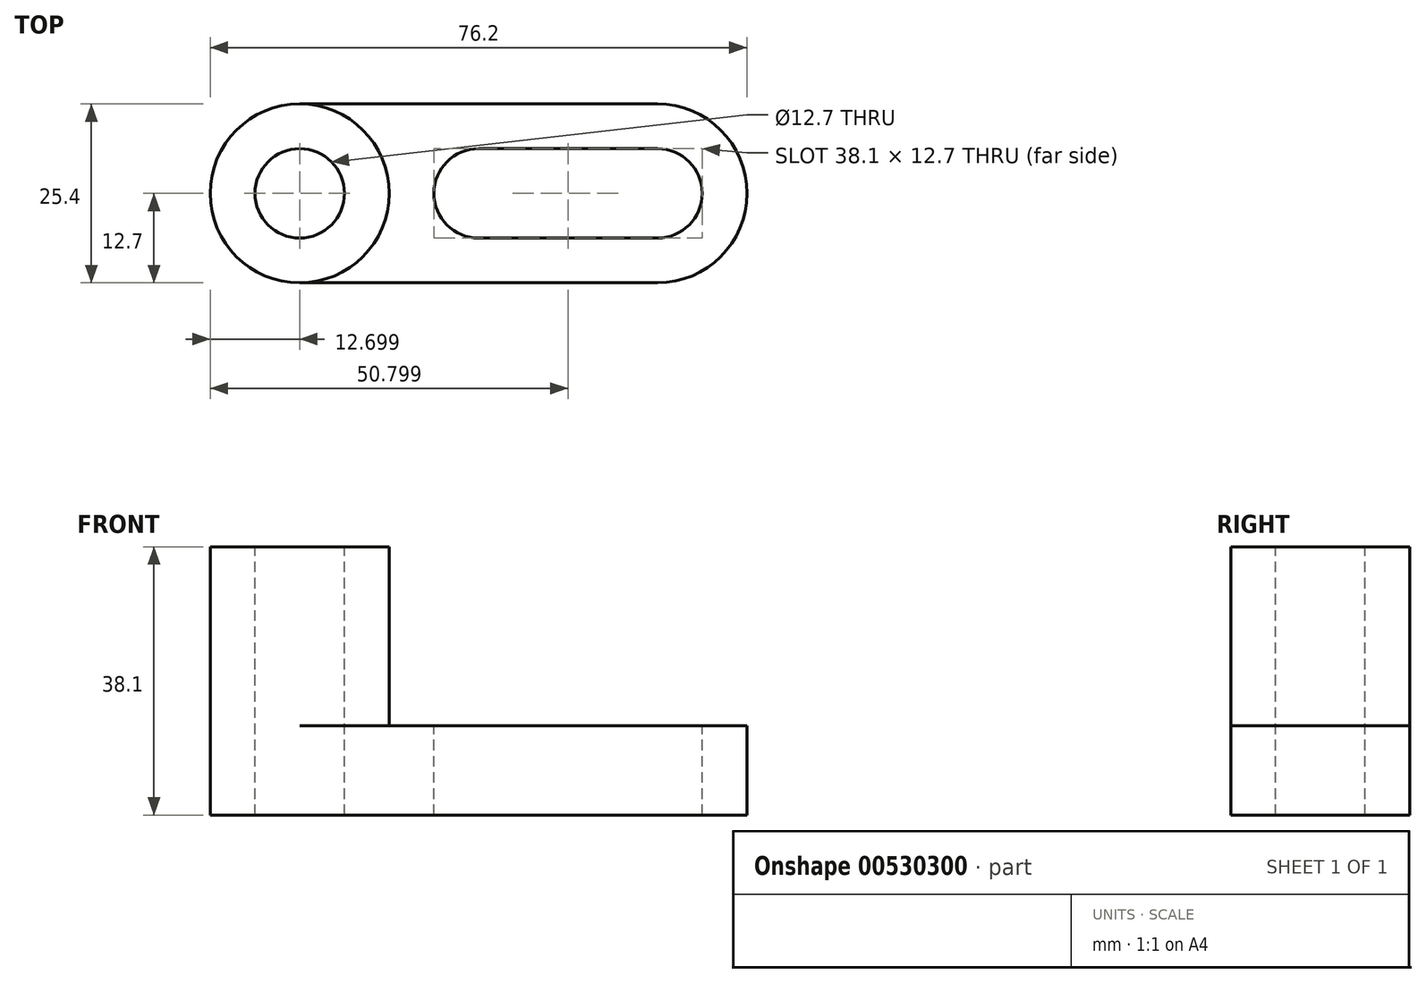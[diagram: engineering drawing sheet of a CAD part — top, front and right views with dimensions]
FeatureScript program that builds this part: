
annotation { "Feature Type Name" : "Feature", "Feature Type Description" : "" }
export const myFeature = defineFeature(function(context is Context, id is Id, definition is map)
    precondition{}
    {
        {
            var Q0;
            Q0=qCreatedBy(makeId("Front.planeOp"),FACE);
            var sketch = newSketch(context, id + "F0", { "sketchPlane" : qUnion([Q0])});
            skLineSegment(sketch, "E0", {"start": v(-38.5, 38.1) * mm, "end": v(-38.5, 0) * mm});
            skLineSegment(sketch, "E1", {"start": v(-38.5, 0) * mm, "end": v(37.7, 0) * mm});
            skLineSegment(sketch, "E2", {"start": v(37.7, 0) * mm, "end": v(37.7, 38.1) * mm});
            skLineSegment(sketch, "E3", {"start": v(-38.5, 38.1) * mm, "end": v(37.7, 38.1) * mm});
            skSolve(sketch);
        }
        {
            var Q0;
            Q0=makeQuery(id+"F0.imprint","IMPRINT",FACE,{"disambiguationData":[TD([[makeQuery(id+"F0.imprint","IMPRINT",EDGE,{"derivedFrom":sQuery(id+"F0.wireOp",EDGE,"E0")}),1.0]])]});
            extrude(context, id + "F1", {"entities" : qUnion([Q0]), "depth" : 25.4 * mm, "offsetDistance" : 25.4 * mm});
        }
        {
            var Q0;
            Q0=makeQuery(id+"F1.opExtrude","SWEPT_FACE",FACE,{"disambiguationData":[OSD([sQuery(id+"F0.wireOp",EDGE,"E3")])]});
            var sketch = newSketch(context, id + "F2", { "sketchPlane" : qUnion([Q0])});
            skCircle(sketch, "E4", {"center": v(-25.8, -12.7) * mm, "radius": 12.7 * mm});
            skSolve(sketch);
        }
        {
            var Q0;
            {var subQ1=sQuery(id+"F0.wireOp",EDGE,"E3");var subQ6=makeQuery(id+"F1.opExtrude","SWEPT_EDGE",EDGE,{"disambiguationData":[OSD([sQuery(id+"F0.wireOp",EDGE,"E2"),subQ1])]});Q0=makeQuery(id+"F2.imprint","IMPRINT",FACE,{"disambiguationData":[TD([[makeQuery(id+"F2.imprint","IMPRINT",EDGE,{"derivedFrom":subQ6}),1.0]])]});}
            var Q1;
            {var subQ0=sQuery(id+"F2.wireOp",EDGE,"E4");var subQ1=sQuery(id+"F0.wireOp",EDGE,"E3");var subQ4=makeQuery(id+"F1.opExtrude","CAP_EDGE",EDGE,{"disambiguationData":[OSD([subQ1])],"isStart":true});var subQ5=makeQuery(id+"F2.imprint","INTERSECT",VERTEX,{"derivedFrom":[subQ4,subQ0]});Q1=makeQuery(id+"F2.imprint","IMPRINT",FACE,{"disambiguationData":[TD([[makeQuery(id+"F2.imprint","IMPRINT",EDGE,{"disambiguationData":[TD([[subQ5,-1.0]])],"derivedFrom":subQ0}),-1.0]])]});}
            var Q2;
            {var subQ0=sQuery(id+"F2.wireOp",EDGE,"E4");var subQ1=sQuery(id+"F0.wireOp",EDGE,"E3");var subQ4=makeQuery(id+"F1.opExtrude","CAP_EDGE",EDGE,{"disambiguationData":[OSD([subQ1])],"isStart":false});var subQ5=makeQuery(id+"F2.imprint","INTERSECT",VERTEX,{"derivedFrom":[subQ4,subQ0]});Q2=makeQuery(id+"F2.imprint","IMPRINT",FACE,{"disambiguationData":[TD([[makeQuery(id+"F2.imprint","IMPRINT",EDGE,{"disambiguationData":[TD([[subQ5,1.0]])],"derivedFrom":subQ0}),-1.0]])]});}
            extrude(context, id + "F3", {"entities" : qUnion([Q0, Q1, Q2]), "operationType" : NewBodyOperationType.REMOVE, "oppositeDirection" : true, "depth" : 25.4 * mm, "offsetDistance" : 25.4 * mm});
        }
        {
            var Q0;
            {var subQ0=sQuery(id+"F0.wireOp",EDGE,"E3");var subQ1=makeQuery(id+"F1.opExtrude","CAP_EDGE",EDGE,{"disambiguationData":[OSD([subQ0])],"isStart":true});var subQ2=sQuery(id+"F0.wireOp",EDGE,"E0");var subQ3=makeQuery(id+"F1.opExtrude","SWEPT_EDGE",EDGE,{"disambiguationData":[OSD([subQ2,subQ0])]});var subQ4=makeQuery(id+"F2.imprint","INTERSECT",VERTEX,{"derivedFrom":[subQ3,subQ1]});var subQ5=sQuery(id+"F2.wireOp",EDGE,"E4");var subQ6=makeQuery(id+"F2.imprint","INTERSECT",VERTEX,{"derivedFrom":[subQ1,subQ5]});Q0=makeQuery(id+"F3.boolean.opBoolean","COPY",FACE,{"derivedFrom":makeQuery(id+"F3.opExtrude","CAP_FACE",FACE,{"disambiguationData":[OSD([subQ2,subQ0,subQ5]),TDD([makeQuery(id+"F2.imprint","IMPRINT",EDGE,{"disambiguationData":[TD([[subQ6,-1.0]])],"derivedFrom":subQ5}),makeQuery(id+"F2.imprint","IMPRINT",EDGE,{"disambiguationData":[TD([[subQ4,1.0]])],"derivedFrom":subQ3}),makeQuery(id+"F2.imprint","IMPRINT",EDGE,{"disambiguationData":[TD([[subQ6,1.0]])],"derivedFrom":subQ1})])],"isStart":false})});}
            var Q1;
            {var subQ0=sQuery(id+"F0.wireOp",EDGE,"E3");var subQ1=makeQuery(id+"F1.opExtrude","CAP_EDGE",EDGE,{"disambiguationData":[OSD([subQ0])],"isStart":false});var subQ2=sQuery(id+"F0.wireOp",EDGE,"E0");var subQ3=makeQuery(id+"F1.opExtrude","SWEPT_EDGE",EDGE,{"disambiguationData":[OSD([subQ2,subQ0])]});var subQ4=makeQuery(id+"F2.imprint","INTERSECT",VERTEX,{"derivedFrom":[subQ3,subQ1]});var subQ5=sQuery(id+"F2.wireOp",EDGE,"E4");var subQ6=makeQuery(id+"F2.imprint","INTERSECT",VERTEX,{"derivedFrom":[subQ1,subQ5]});Q1=makeQuery(id+"F3.boolean.opBoolean","COPY",FACE,{"derivedFrom":makeQuery(id+"F3.opExtrude","CAP_FACE",FACE,{"disambiguationData":[OSD([subQ2,subQ0,subQ5]),TDD([makeQuery(id+"F2.imprint","IMPRINT",EDGE,{"disambiguationData":[TD([[subQ6,1.0]])],"derivedFrom":subQ5}),makeQuery(id+"F2.imprint","IMPRINT",EDGE,{"disambiguationData":[TD([[subQ4,-1.0]])],"derivedFrom":subQ3}),makeQuery(id+"F2.imprint","IMPRINT",EDGE,{"disambiguationData":[TD([[subQ6,1.0]])],"derivedFrom":subQ1})])],"isStart":false})});}
            extrude(context, id + "F4", {"entities" : qUnion([Q0, Q1]), "operationType" : NewBodyOperationType.REMOVE, "endBound" : BoundingType.THROUGH_ALL, "oppositeDirection" : true, "depth" : 25.4 * mm, "offsetDistance" : 25.4 * mm});
        }
        {
            var Q0;
            Q0=makeQuery(id+"F1.opExtrude","SWEPT_FACE",FACE,{"disambiguationData":[OSD([sQuery(id+"F0.wireOp",EDGE,"E3")])]});
            var sketch = newSketch(context, id + "F5", { "sketchPlane" : qUnion([Q0])});
            skCircle(sketch, "E5", {"center": v(-25.8, -12.7) * mm, "radius": 6.35 * mm});
            skSolve(sketch);
        }
        {
            var Q0;
            Q0=makeQuery(id+"F5.imprint","IMPRINT",FACE,{"disambiguationData":[TD([[makeQuery(id+"F5.imprint","IMPRINT",EDGE,{"derivedFrom":sQuery(id+"F5.wireOp",EDGE,"E5")}),1.0]])]});
            extrude(context, id + "F6", {"entities" : qUnion([Q0]), "operationType" : NewBodyOperationType.REMOVE, "endBound" : BoundingType.THROUGH_ALL, "oppositeDirection" : true, "depth" : 25.4 * mm, "offsetDistance" : 25.4 * mm});
        }
        {
            var Q0;
            Q0=makeQuery(id+"F3.boolean.opBoolean","COPY",FACE,{"derivedFrom":makeQuery(id+"F3.opExtrude","CAP_FACE",FACE,{"disambiguationData":[OSD([sQuery(id+"F0.wireOp",EDGE,"E2"),sQuery(id+"F0.wireOp",EDGE,"E3"),sQuery(id+"F2.wireOp",EDGE,"E4")])],"isStart":false})});
            var sketch = newSketch(context, id + "F7", { "sketchPlane" : qUnion([Q0])});
            skCircle(sketch, "E6", {"center": v(25, -12.7) * mm, "radius": 6.35 * mm});
            skCircle(sketch, "E7", {"center": v(-0.4, -12.7) * mm, "radius": 6.35 * mm});
            skLineSegment(sketch, "E8", {"start": v(-0.4, -12.7) * mm, "end": v(-0.4, -25.4) * mm});
            skLineSegment(sketch, "E9", {"start": v(-0.4, -6.35) * mm, "end": v(25, -6.35) * mm});
            skLineSegment(sketch, "E10", {"start": v(25, -19.05) * mm, "end": v(-0.4, -19.05) * mm});
            skLineSegment(sketch, "E11", {"start": v(25, -12.7) * mm, "end": v(37.7, -12.7) * mm});
            skArc(sketch, "E12", {"start": v(25, -25.4) * mm, "mid": v(37.7, -12.7) * mm, "end": v(25, 0) * mm});
            skSolve(sketch);
        }
        {
            var Q0;
            {var subQ0=sQuery(id+"F7.wireOp",EDGE,"E7");var subQ1=makeQuery(id+"F7.imprint","INTERSECT",VERTEX,{"derivedFrom":[subQ0,sQuery(id+"F7.wireOp",EDGE,"E9")]});Q0=makeQuery(id+"F7.imprint","IMPRINT",FACE,{"disambiguationData":[TD([[makeQuery(id+"F7.imprint","IMPRINT",EDGE,{"disambiguationData":[TD([[subQ1,-1.0]])],"derivedFrom":subQ0}),1.0]])]});}
            var Q1;
            {var subQ0=sQuery(id+"F7.wireOp",EDGE,"E9");Q1=makeQuery(id+"F7.imprint","IMPRINT",FACE,{"disambiguationData":[TD([[makeQuery(id+"F7.imprint","IMPRINT",EDGE,{"derivedFrom":subQ0}),-1.0]])]});}
            var Q2;
            {var subQ0=sQuery(id+"F7.wireOp",EDGE,"E6");var subQ1=makeQuery(id+"F7.imprint","INTERSECT",VERTEX,{"derivedFrom":[subQ0,sQuery(id+"F7.wireOp",EDGE,"E9")]});Q2=makeQuery(id+"F7.imprint","IMPRINT",FACE,{"disambiguationData":[TD([[makeQuery(id+"F7.imprint","IMPRINT",EDGE,{"disambiguationData":[TD([[subQ1,1.0]])],"derivedFrom":subQ0}),1.0]])]});}
            var Q3;
            {var subQ0=sQuery(id+"F7.wireOp",EDGE,"E12");var subQ1=sQuery(id+"F0.wireOp",EDGE,"E3");var subQ5=makeQuery(id+"F1.opExtrude","CAP_EDGE",EDGE,{"disambiguationData":[OSD([subQ1])],"isStart":false});var subQ6=makeQuery(id+"F3.boolean.opBoolean","COPY",EDGE,{"derivedFrom":makeQuery(id+"F3.opExtrude","CAP_EDGE",EDGE,{"disambiguationData":[OSD([subQ1]),TDD([makeQuery(id+"F2.imprint","IMPRINT",EDGE,{"disambiguationData":[TD([[makeQuery(id+"F2.imprint","INTERSECT",VERTEX,{"derivedFrom":[subQ5,sQuery(id+"F2.wireOp",EDGE,"E4")]}),-1.0]])],"derivedFrom":subQ5})])],"isStart":false})});var subQ7=makeQuery(id+"F7.imprint","INTERSECT",VERTEX,{"derivedFrom":[subQ6,subQ0]});Q3=makeQuery(id+"F7.imprint","IMPRINT",FACE,{"disambiguationData":[TD([[makeQuery(id+"F7.imprint","IMPRINT",EDGE,{"disambiguationData":[TD([[subQ7,-1.0]])],"derivedFrom":subQ0}),-1.0]])]});}
            var Q4;
            {var subQ0=sQuery(id+"F7.wireOp",EDGE,"E12");var subQ1=sQuery(id+"F0.wireOp",EDGE,"E3");var subQ5=makeQuery(id+"F1.opExtrude","CAP_EDGE",EDGE,{"disambiguationData":[OSD([subQ1])],"isStart":true});var subQ6=makeQuery(id+"F3.boolean.opBoolean","COPY",EDGE,{"derivedFrom":makeQuery(id+"F3.opExtrude","CAP_EDGE",EDGE,{"disambiguationData":[OSD([subQ1]),TDD([makeQuery(id+"F2.imprint","IMPRINT",EDGE,{"disambiguationData":[TD([[makeQuery(id+"F2.imprint","INTERSECT",VERTEX,{"derivedFrom":[subQ5,sQuery(id+"F2.wireOp",EDGE,"E4")]}),-1.0]])],"derivedFrom":subQ5})])],"isStart":false})});var subQ7=makeQuery(id+"F7.imprint","INTERSECT",VERTEX,{"derivedFrom":[subQ6,subQ0]});Q4=makeQuery(id+"F7.imprint","IMPRINT",FACE,{"disambiguationData":[TD([[makeQuery(id+"F7.imprint","IMPRINT",EDGE,{"disambiguationData":[TD([[subQ7,1.0]])],"derivedFrom":subQ0}),-1.0]])]});}
            extrude(context, id + "F8", {"entities" : qUnion([Q0, Q1, Q2, Q3, Q4]), "operationType" : NewBodyOperationType.REMOVE, "endBound" : BoundingType.THROUGH_ALL, "oppositeDirection" : true, "depth" : 25.4 * mm, "offsetDistance" : 25.4 * mm});
        }
    });
